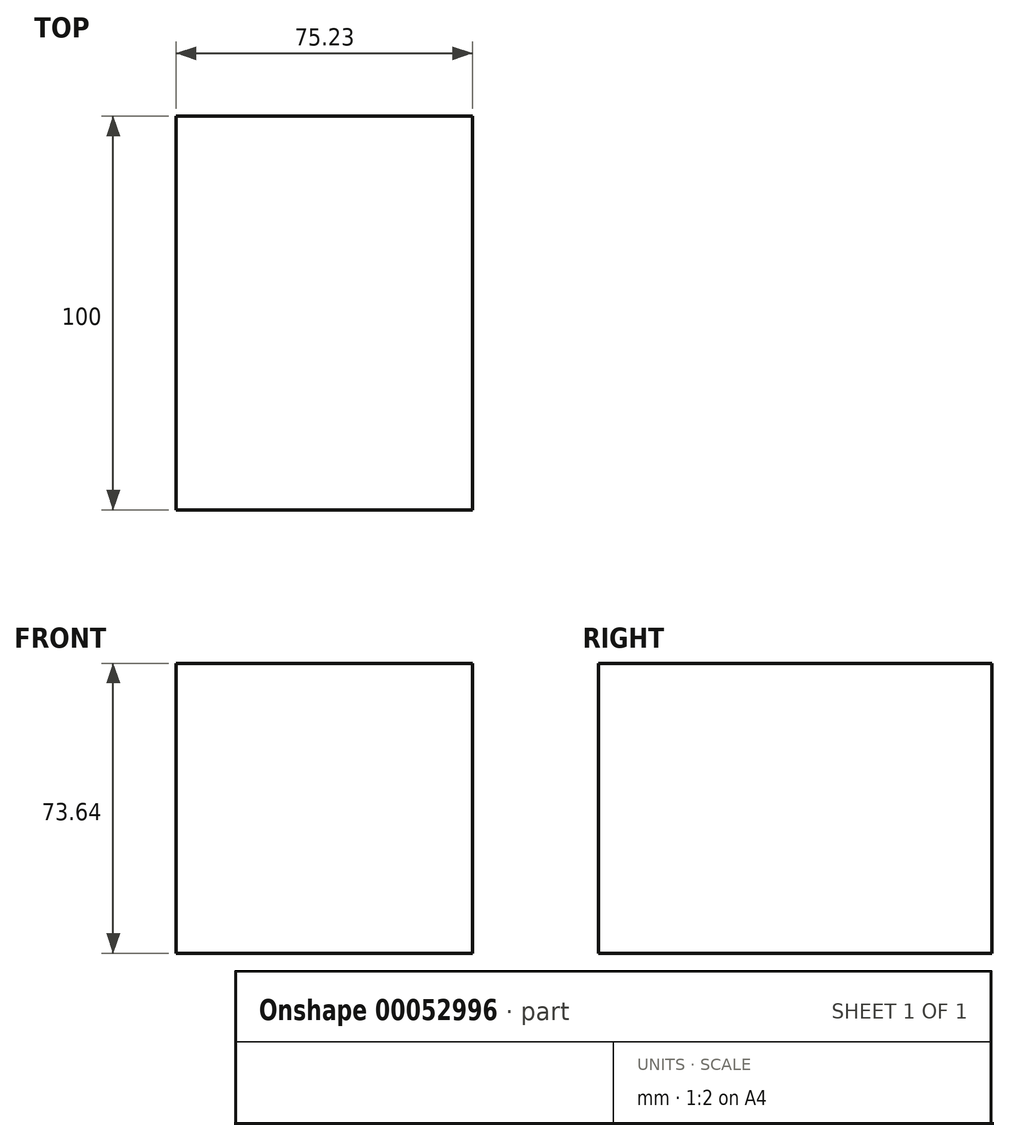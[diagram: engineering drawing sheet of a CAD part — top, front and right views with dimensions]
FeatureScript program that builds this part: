
annotation { "Feature Type Name" : "Feature", "Feature Type Description" : "" }
export const myFeature = defineFeature(function(context is Context, id is Id, definition is map)
    precondition{}
    {
        {
            var Q0;
            Q0=qCreatedBy(makeId("Front.planeOp"),FACE);
            var sketch = newSketch(context, id + "F0", { "sketchPlane" : qUnion([Q0])});
            skLineSegment(sketch, "E0.bottom", {"start": v(0, 0) * mm, "end": v(-75.23, 0) * mm});
            skLineSegment(sketch, "E0.top", {"start": v(0, 73.64) * mm, "end": v(-75.23, 73.64) * mm});
            skLineSegment(sketch, "E0.left", {"start": v(0, 0) * mm, "end": v(0, 73.64) * mm});
            skLineSegment(sketch, "E0.right", {"start": v(-75.23, 0) * mm, "end": v(-75.23, 73.64) * mm});
            skSolve(sketch);
        }
        {
            var Q0;
            Q0=makeQuery(id+"F0.imprint","IMPRINT",FACE,{"disambiguationData":[TD([[makeQuery(id+"F0.imprint","IMPRINT",EDGE,{"derivedFrom":sQuery(id+"F0.wireOp",EDGE,"E0.bottom")}),-1.0]])]});
            extrude(context, id + "F1", {"entities" : qUnion([Q0]), "depth" : 100 * mm});
        }
        {
            var Q0;
            Q0=makeQuery(id+"F1.opExtrude","CAP_FACE",FACE,{"disambiguationData":[OSD([sQuery(id+"F0.wireOp",EDGE,"E0.bottom"),sQuery(id+"F0.wireOp",EDGE,"E0.top"),sQuery(id+"F0.wireOp",EDGE,"E0.left"),sQuery(id+"F0.wireOp",EDGE,"E0.right")])],"isStart":false});
            var sketch = newSketch(context, id + "F2", { "sketchPlane" : qUnion([Q0])});
            skCircle(sketch, "E1", {"center": v(-41.99, 33.4) * mm, "radius": 26.8 * mm});
            skCircle(sketch, "E2", {"center": v(-41.99, 33.4) * mm, "radius": 13.26 * mm});
            skSolve(sketch);
        }
        {
            var Q0;
            Q0 = qSketchRegion(id + "F2", true);
            extrude(context, id + "F3", {"entities" : qUnion([Q0]), "operationType" : NewBodyOperationType.ADD, "oppositeDirection" : true, "depth" : 75 * mm});
        }
        {
            var Q0;
            Q0=makeQuery(id+"F1.opExtrude","CAP_FACE",FACE,{"disambiguationData":[OSD([sQuery(id+"F0.wireOp",EDGE,"E0.bottom"),sQuery(id+"F0.wireOp",EDGE,"E0.top"),sQuery(id+"F0.wireOp",EDGE,"E0.left"),sQuery(id+"F0.wireOp",EDGE,"E0.right")])],"isStart":false});
            var sketch = newSketch(context, id + "F4", { "sketchPlane" : qUnion([Q0])});
            skCircle(sketch, "E3", {"center": v(-41.34, 35.24) * mm, "radius": 26.32 * mm});
            skSolve(sketch);
        }
        {
            var Q0;
            Q0=makeQuery(id+"F4.imprint","IMPRINT",FACE,{"disambiguationData":[TD([[makeQuery(id+"F4.imprint","IMPRINT",EDGE,{"derivedFrom":sQuery(id+"F4.wireOp",EDGE,"E3")}),1.0]])]});
            extrude(context, id + "F5", {"entities" : qUnion([Q0]), "operationType" : NewBodyOperationType.ADD, "oppositeDirection" : true, "depth" : 50 * mm});
        }
    });
